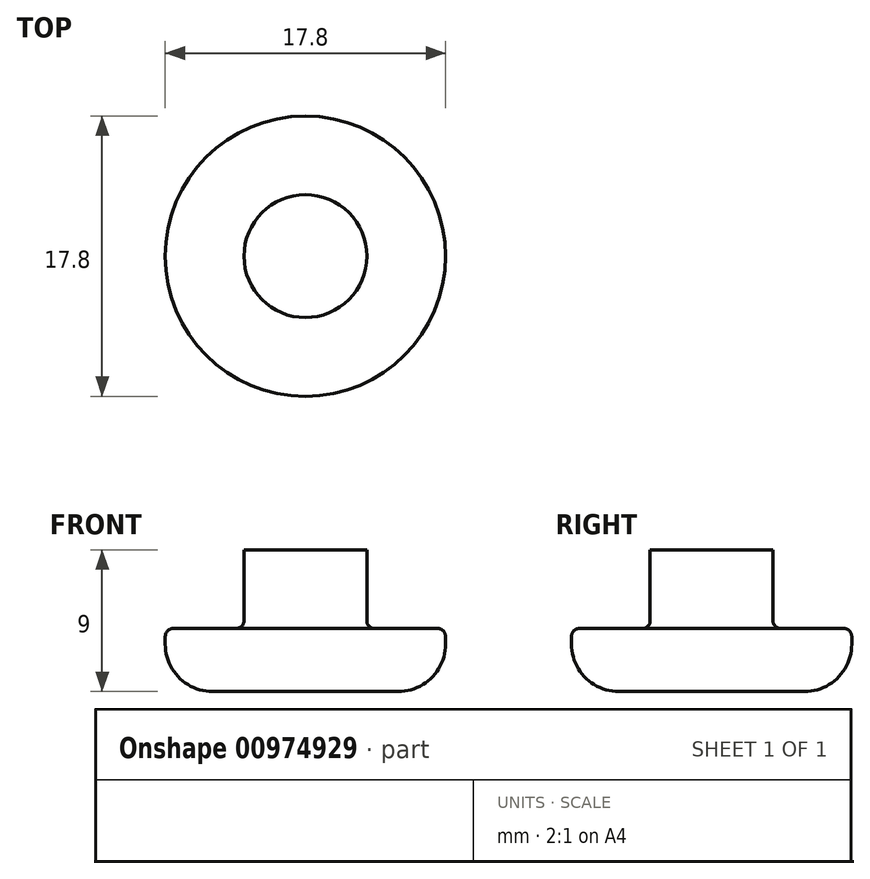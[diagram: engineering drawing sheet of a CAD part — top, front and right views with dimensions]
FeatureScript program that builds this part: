
annotation { "Feature Type Name" : "Feature", "Feature Type Description" : "" }
export const myFeature = defineFeature(function(context is Context, id is Id, definition is map)
    precondition{}
    {
        {
            var Q0;
            Q0=qCreatedBy(makeId("Front.planeOp"),FACE);
            var sketch = newSketch(context, id + "F0", { "sketchPlane" : qUnion([Q0])});
            skLineSegment(sketch, "E0", {"start": v(-6.65, -14.39) * mm, "end": v(-11.65, -14.39) * mm});
            skLineSegment(sketch, "E1", {"start": v(-2.75, -18.39) * mm, "end": v(-11.65, -18.39) * mm});
            skLineSegment(sketch, "E2", {"start": v(-11.65, -18.39) * mm, "end": v(-11.65, -14.39) * mm});
            skLineSegment(sketch, "E3", {"start": v(-6.65, -14.39) * mm, "end": v(-6.65, -9.39) * mm});
            skLineSegment(sketch, "E4", {"start": v(-6.65, -9.39) * mm, "end": v(-2.75, -9.39) * mm});
            skLineSegment(sketch, "E5", {"start": v(-2.75, -9.39) * mm, "end": v(-2.75, -18.39) * mm});
            skSolve(sketch);
        }
        {
            var Q0;
            Q0=makeQuery(id+"F0.imprint","IMPRINT",FACE,{"disambiguationData":[TD([[makeQuery(id+"F0.imprint","IMPRINT",EDGE,{"derivedFrom":sQuery(id+"F0.wireOp",EDGE,"E0")}),1.0]])]});
            var Q1;
            Q1=sQuery(id+"F0.wireOp",EDGE,"E5");
            revolve(context, id + "F1", {"surfaceOperationType" : NewSurfaceOperationType.NEW, "entities" : qUnion([Q0]), "axis" : qUnion([Q1]), "revolveType" : RevolveType.FULL});
        }
        {
            var Q0;
            Q0=makeQuery(id+"F1.opRevolve","SWEPT_EDGE",EDGE,{"disambiguationData":[OSD([sQuery(id+"F0.wireOp",EDGE,"E0"),sQuery(id+"F0.wireOp",EDGE,"4JXChL0u-YRMm-ED8T-Iymw-Wsi0TD2Kl2xh")])]});
            var Q1;
            Q1=makeQuery(id+"F1.opRevolve","SWEPT_EDGE",EDGE,{"disambiguationData":[OSD([sQuery(id+"F0.wireOp",EDGE,"4JXChL0u-YRMm-ED8T-Iymw-Wsi0TD2Kl2xh"),sQuery(id+"F0.wireOp",EDGE,"jWw1U1Bi-CT9r-OHnl-7njm-QvZPqrv6GL0x")])]});
            fillet(context, id + "F2", {"entities" : qUnion([Q0, Q1]), "radius" : 0.5 * mm, "tangentPropagation" : true, "allowEdgeOverflow" : false});
        }
        {
            var Q0;
            Q0=makeQuery(id+"F1.opRevolve","SWEPT_EDGE",EDGE,{"disambiguationData":[OSD([sQuery(id+"F0.wireOp",EDGE,"E1"),sQuery(id+"F0.wireOp",EDGE,"E2")])]});
            fillet(context, id + "F3", {"entities" : qUnion([Q0]), "radius" : 3 * mm, "tangentPropagation" : true, "allowEdgeOverflow" : false});
        }
    });
